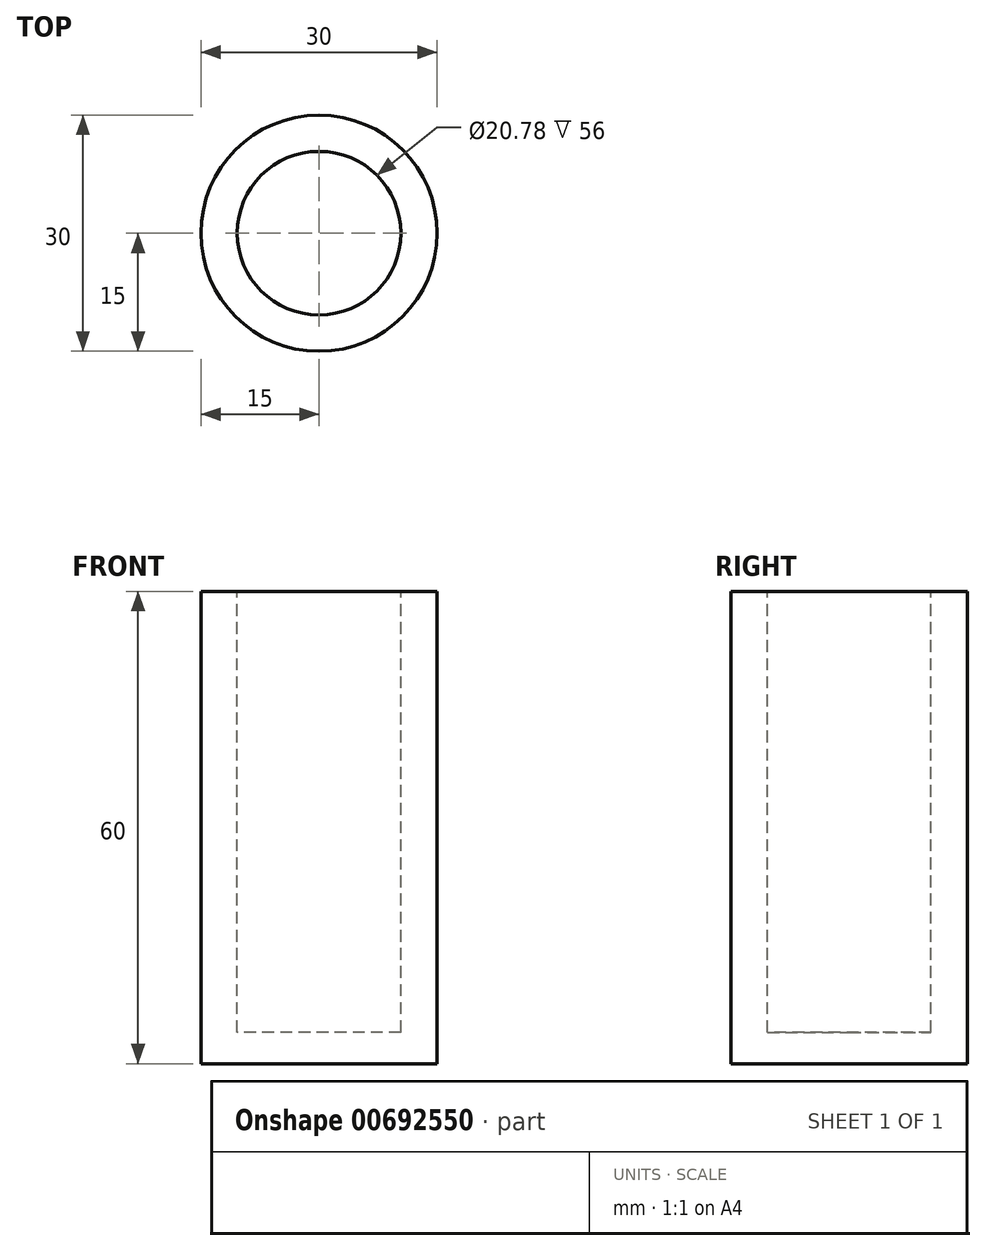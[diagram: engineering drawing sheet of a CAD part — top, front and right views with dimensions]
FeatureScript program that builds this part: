
annotation { "Feature Type Name" : "Feature", "Feature Type Description" : "" }
export const myFeature = defineFeature(function(context is Context, id is Id, definition is map)
    precondition{}
    {
        {
            var Q0;
            Q0=qCreatedBy(makeId("Top.planeOp"),FACE);
            var sketch = newSketch(context, id + "F0", { "sketchPlane" : qUnion([Q0])});
            skCircle(sketch, "E0", {"center": v(0, 0) * mm, "radius": 15 * mm});
            skSolve(sketch);
        }
        {
            var Q0;
            Q0 = qSketchRegion(id + "F0", true);
            extrude(context, id + "F1", {"entities" : qUnion([Q0]), "depth" : 60 * mm, "offsetDistance" : 25 * mm});
        }
        {
            var Q0;
            Q0=makeQuery(id+"F1.opExtrude","CAP_FACE",FACE,{"disambiguationData":[OSD([sQuery(id+"F0.wireOp",EDGE,"E0")])],"isStart":false});
            var sketch = newSketch(context, id + "F2", { "sketchPlane" : qUnion([Q0])});
            skCircle(sketch, "E1", {"center": v(0, 0) * mm, "radius": 10.4 * mm});
            skSolve(sketch);
        }
        {
            var Q0;
            Q0=makeQuery(id+"F2.imprint","IMPRINT",FACE,{"disambiguationData":[TD([[makeQuery(id+"F2.imprint","IMPRINT",EDGE,{"derivedFrom":sQuery(id+"F2.wireOp",EDGE,"E1")}),1.0]])]});
            extrude(context, id + "F3", {"entities" : qUnion([Q0]), "operationType" : NewBodyOperationType.REMOVE, "depth" : -56 * mm, "offsetDistance" : 25 * mm});
        }
    });
